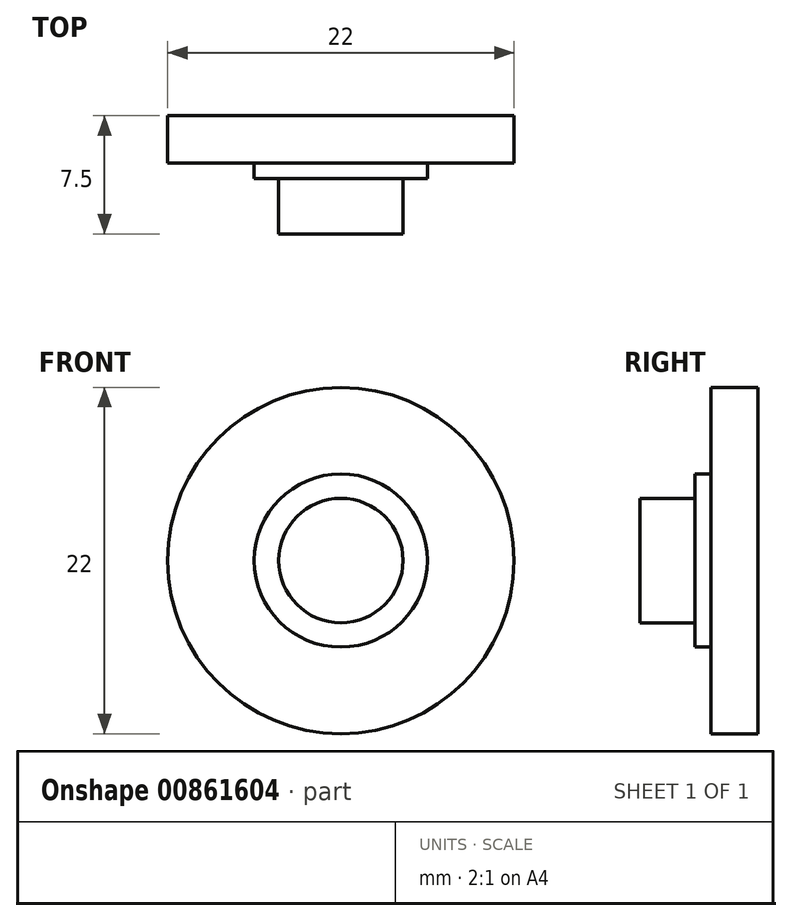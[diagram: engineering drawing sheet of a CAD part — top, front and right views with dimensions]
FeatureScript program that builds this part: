
annotation { "Feature Type Name" : "Feature", "Feature Type Description" : "" }
export const myFeature = defineFeature(function(context is Context, id is Id, definition is map)
    precondition{}
    {
        {
            var Q0;
            Q0=qCreatedBy(makeId("Top.planeOp"),FACE);
            var sketch = newSketch(context, id + "F0", { "sketchPlane" : qUnion([Q0])});
            skLineSegment(sketch, "E0", {"start": v(0, 0) * mm, "end": v(-3.95, 0) * mm});
            skLineSegment(sketch, "E1", {"start": v(-3.95, 0) * mm, "end": v(-3.95, 3.5) * mm});
            skLineSegment(sketch, "E2", {"start": v(-3.95, 3.5) * mm, "end": v(-5.5, 3.5) * mm});
            skLineSegment(sketch, "E3", {"start": v(-5.5, 3.5) * mm, "end": v(-5.5, 4.5) * mm});
            skLineSegment(sketch, "E4", {"start": v(0, 0) * mm, "end": v(0, 7.5) * mm});
            skLineSegment(sketch, "E5", {"start": v(0, 7.5) * mm, "end": v(-11, 7.5) * mm});
            skLineSegment(sketch, "E6", {"start": v(-11, 7.5) * mm, "end": v(-11, 4.5) * mm});
            skLineSegment(sketch, "E7", {"start": v(-11, 4.5) * mm, "end": v(-5.5, 4.5) * mm});
            skSolve(sketch);
        }
        {
            var Q0;
            Q0=makeQuery(id+"F0.imprint","IMPRINT",FACE,{"disambiguationData":[TD([[makeQuery(id+"F0.imprint","IMPRINT",EDGE,{"derivedFrom":sQuery(id+"F0.wireOp",EDGE,"E0")}),-1.0]])]});
            var Q1;
            Q1=sQuery(id+"F0.wireOp",EDGE,"E4");
            revolve(context, id + "F1", {"surfaceOperationType" : NewSurfaceOperationType.NEW, "entities" : qUnion([Q0]), "axis" : qUnion([Q1]), "revolveType" : RevolveType.FULL});
        }
    });
